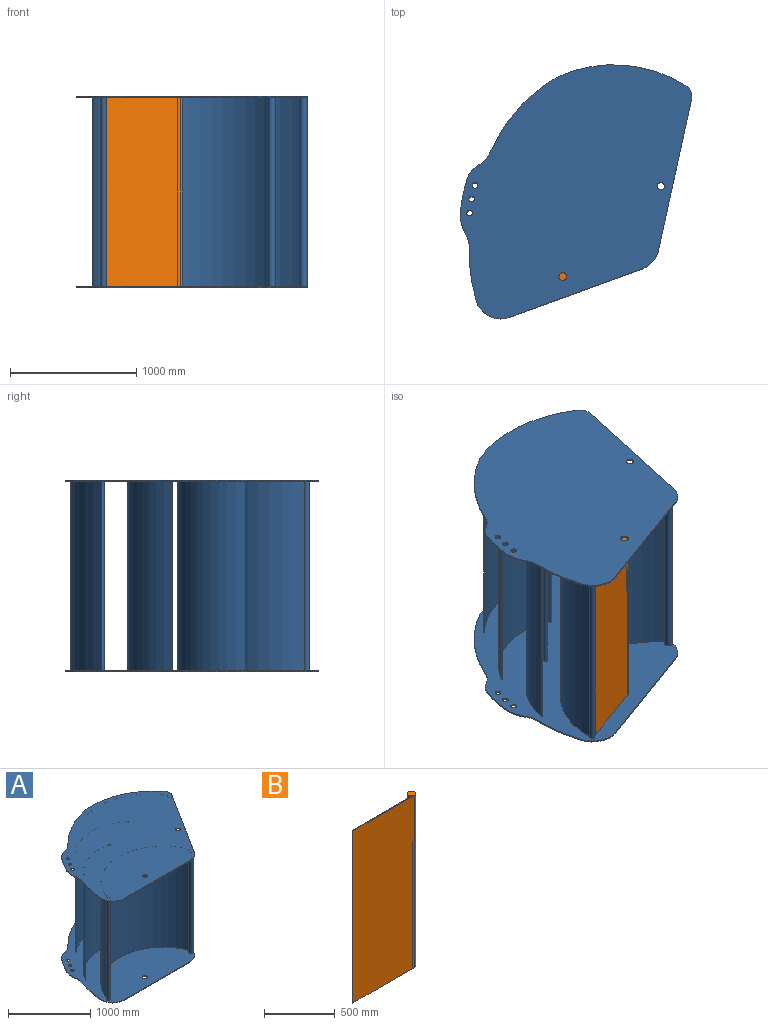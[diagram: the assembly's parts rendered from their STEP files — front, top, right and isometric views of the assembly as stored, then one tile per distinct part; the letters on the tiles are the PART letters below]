
ASSEMBLY  parts=2 mates=2
PART A: 61 faces, bbox 2164.2x1661x1520 mm
  f0: cylinder r=30.5mm len=61mm, axis (0,0,-1), area 1916.4mm2, adj f48,f49
  f1: cylinder r=29.5mm len=59mm, axis (0,0,-1), area 1853.5mm2, adj f48,f49
  f2: cylinder r=22mm len=44mm, axis (0,0,-1), area 1382.3mm2, adj f48,f49
  f3: cylinder r=22mm len=44mm, axis (0,0,-1), area 1382.3mm2, adj f48,f49
  f4: cylinder r=22mm len=44mm, axis (0,0,-1), area 1382.3mm2, adj f48,f49
  f5: cylinder r=326.18mm len=176.61mm, axis (0,0,-1), area 1797.7mm2, adj f48,f49,f50,f60
  f6: cylinder r=200mm len=212.82mm, axis (0,0,-1), area 3269.9mm2, adj f48,f49,f51,f52
  f7: cylinder r=20.5mm len=1500mm, axis (0,0,-1), area 183146.8mm2, adj f30,f44,f45,f49
  f8: cylinder r=30.5mm len=1500mm, axis (0,0,-1), area 272705.4mm2, adj f30,f44,f45,f46,f47,f49
  f9: cylinder r=15.5mm len=1500mm, axis (0,0,-1), area 135747.8mm2, adj f30,f41,f43,f49
  f10: cylinder r=15.5mm len=1500mm, axis (0,0,-1), area 136340.4mm2, adj f30,f37,f40,f49
  f11: cylinder r=30.5mm len=1500mm, axis (0,0,-1), area 274743.1mm2, adj f30,f32,f34,f35,f36,f49
  f12: cylinder r=30.5mm len=61mm, axis (0,0,-1), area 1916.4mm2, adj f30,f31
  f13: cylinder r=22mm len=44mm, axis (0,0,-1), area 1382.3mm2, adj f30,f31
  f14: cylinder r=22mm len=44mm, axis (0,0,-1), area 1382.3mm2, adj f30,f31
  f15: cylinder r=22mm len=44mm, axis (0,0,-1), area 1382.3mm2, adj f30,f31
  f16: cylinder r=29.5mm len=59mm, axis (0,0,-1), area 1853.5mm2, adj f30,f31
  f17: cylinder r=326.18mm len=176.61mm, axis (0,0,-1), area 1797.7mm2, adj f28,f29,f30,f31
  f18: cylinder r=200mm len=212.82mm, axis (0,0,-1), area 3269.9mm2, adj f19,f20,f30,f31
  f19: cylinder r=1403.06mm len=415.74mm, axis (0,0,-1), area 4273.2mm2, adj f18,f29,f30,f31
  f20: plane 1123.76x10mm, normal (0,-1,0), area 11237.6mm2, adj f18,f21,f30,f31
  f21: cylinder r=200mm len=169mm, axis (0,0,-1), area 2013.2mm2, adj f20,f22,f30,f31
  f22: plane 1036.5x655.9mm, normal (0.85,-0.53,0), area 12265.9mm2, adj f21,f23,f30,f31,f36,f47
  f23: cylinder r=100mm len=114.68mm, axis (0,0,-1), area 1222.9mm2, adj f22,f24,f30,f31
  f24: cylinder r=1074.34mm len=926.41mm, axis (0,0,-1), area 10568mm2, adj f23,f25,f30,f31
  f25: cylinder r=1282.61mm len=713.26mm, axis (0,0,-1), area 8227.7mm2, adj f24,f26,f30,f31
  f26: cylinder r=200mm len=117.51mm, axis (0,0,-1), area 1346.6mm2, adj f25,f27,f30,f31
  f27: cylinder r=186.95mm len=116.81mm, axis (0,0,-1), area 1363.1mm2, adj f26,f28,f30,f31
  f28: cylinder r=1324.47mm len=239.75mm, axis (0,0,-1), area 2828.3mm2, adj f17,f27,f30,f31
  f29: cylinder r=200mm len=107.43mm, axis (0,0,-1), area 1093.1mm2, adj f17,f19,f30,f31
  f30: plane 2164.16x1660.98mm, normal (0,0,1), area 2565292.9mm2, adj f7,f8,f9,f10,f11,f12,f13,f14
  f31: plane 2164.16x1660.98mm, normal (0,0,-1), area 2603609.2mm2, adj f12,f13,f14,f15,f16,f17,f18,f19
  f32: cylinder r=883.17mm len=1500mm, axis (0,0,-1), area 1936048.7mm2, adj f11,f30,f33,f49
  f33: plane 1500x5.5mm, normal (-0.92,-0.4,0), area 9000mm2, adj f30,f32,f34,f49
  f34: cylinder r=877.17mm len=1500mm, axis (0,0,-1), area 1914005.6mm2, adj f11,f30,f33,f49
  f35: plane 9.3x5.88mm, normal (0,0,1), area 3.7mm2, adj f11,f54
  f36: plane 9.3x5.88mm, normal (0,0,-1), area 3.7mm2, adj f11,f22
  f37: cylinder r=685.89mm len=1500mm, axis (0,0,-1), area 1444091.5mm2, adj f10,f30,f38,f49
  f38: plane 1500x4.62mm, normal (-0.77,-0.64,0), area 9000mm2, adj f30,f37,f39,f49
  f39: plane 1500x0.08mm, normal (0.65,-0.76,0), area 152.6mm2, adj f30,f38,f40,f49
  f40: cylinder r=679.89mm len=1500mm, axis (0,0,-1), area 1427930.9mm2, adj f10,f30,f39,f49
  f41: cylinder r=640.37mm len=1500mm, axis (0,0,-1), area 1242581.2mm2, adj f9,f30,f42,f49
  f42: plane 1500x5.24mm, normal (-0.49,-0.87,0), area 9000mm2, adj f30,f41,f43,f49
  f43: cylinder r=634.37mm len=1500mm, axis (0,0,-1), area 1226053.6mm2, adj f9,f30,f42,f49
  f44: cylinder r=755.25mm len=1500mm, axis (0,0,-1), area 2799788.5mm2, adj f7,f8,f30,f49
  f45: cylinder r=761.25mm len=1500mm, axis (0,0,-1), area 2838096.4mm2, adj f7,f8,f30,f49
  f46: plane 9.3x5.88mm, normal (0,0,1), area 3.7mm2, adj f8,f54
  f47: plane 9.3x5.88mm, normal (0,0,-1), area 3.7mm2, adj f8,f22
  f48: plane 2164.16x1660.98mm, normal (0,0,1), area 2603609.2mm2, adj f0,f1,f2,f3,f4,f5,f6,f50
  f49: plane 2164.16x1660.98mm, normal (0,0,-1), area 2565292.9mm2, adj f0,f1,f2,f3,f4,f5,f6,f7
  f50: cylinder r=200mm len=107.43mm, axis (0,0,-1), area 1093.1mm2, adj f5,f48,f49,f51
  f51: cylinder r=1403.06mm len=415.74mm, axis (0,0,-1), area 4273.2mm2, adj f6,f48,f49,f50
  f52: plane 1123.76x10mm, normal (0,-1,0), area 11237.6mm2, adj f6,f48,f49,f53
  f53: cylinder r=200mm len=169mm, axis (0,0,-1), area 2013.2mm2, adj f48,f49,f52,f54
  f54: plane 1036.5x655.9mm, normal (0.85,-0.53,0), area 12265.9mm2, adj f35,f46,f48,f49,f53,f55
  f55: cylinder r=100mm len=114.68mm, axis (0,0,-1), area 1222.9mm2, adj f48,f49,f54,f56
  f56: cylinder r=1074.34mm len=926.41mm, axis (0,0,-1), area 10568mm2, adj f48,f49,f55,f57
  f57: cylinder r=1282.61mm len=713.26mm, axis (0,0,-1), area 8227.7mm2, adj f48,f49,f56,f58
  f58: cylinder r=200mm len=117.51mm, axis (0,0,-1), area 1346.6mm2, adj f48,f49,f57,f59
  f59: cylinder r=186.95mm len=116.81mm, axis (0,0,-1), area 1363.1mm2, adj f48,f49,f58,f60
  f60: cylinder r=1324.47mm len=239.75mm, axis (0,0,-1), area 2828.3mm2, adj f5,f48,f49,f59
PART B: 6 faces, bbox 646.3x61x1490 mm
  f0: cylinder r=30.5mm len=1490mm, axis (0,0,-1), area 256544.7mm2, adj f1,f2,f4,f5
  f1: plane 1490x615.77mm, normal (0,-1,0), area 917501.9mm2, adj f0,f3,f4,f5
  f2: plane 1490x597.61mm, normal (0,1,0), area 890434.7mm2, adj f0,f3,f4,f5
  f3: plane 1490x6mm, normal (-1,0,0), area 8940mm2, adj f1,f2,f4,f5
  f4: plane 646.27x61mm, normal (0,0,1), area 6542.9mm2, adj f0,f1,f2,f3
  f5: plane 646.27x61mm, normal (0,0,-1), area 6542.9mm2, adj f0,f1,f2,f3
PLACE A rot(axis=(0,0,1),20deg) t=(0,0,-10)mm
PLACE B rot(axis=(0,0,1),20deg) t=(0,0,-10)mm
MATE planar A.f0 <-> B.f0  axis (0,0,-1) through (-777.23,-716.71,750)mm
MATE revolute A.f0 <-> B.f0  axis (0,0,-1) through (-777.23,-716.71,750)mm
